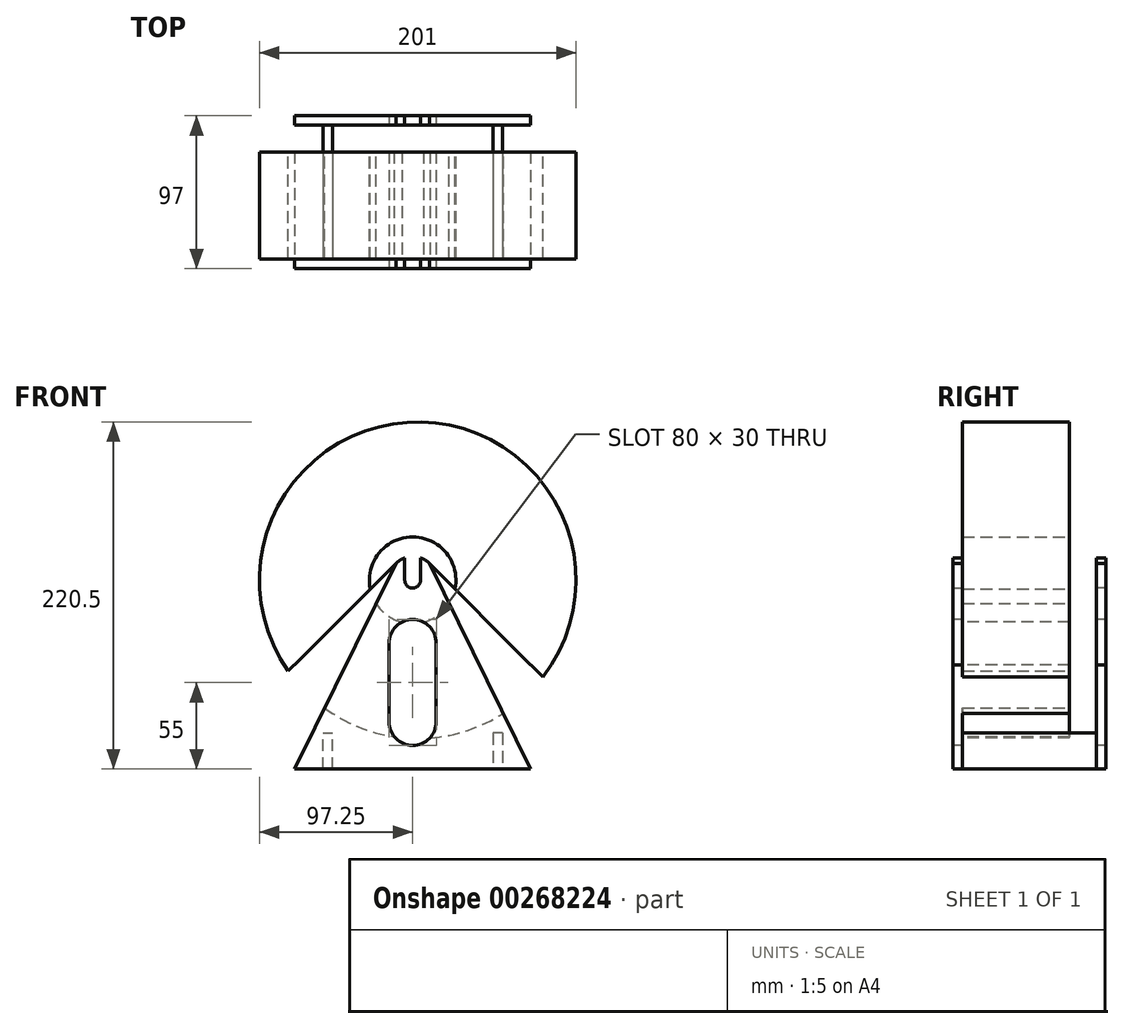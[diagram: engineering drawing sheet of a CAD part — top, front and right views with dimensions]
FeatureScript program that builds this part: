
annotation { "Feature Type Name" : "Feature", "Feature Type Description" : "" }
export const myFeature = defineFeature(function(context is Context, id is Id, definition is map)
    precondition{}
    {
        {
            var Q0;
            Q0=qCreatedBy(makeId("Front.planeOp"),FACE);
            var sketch = newSketch(context, id + "F0", { "sketchPlane" : qUnion([Q0])});
            skCircle(sketch, "E0", {"center": v(0, 0) * mm, "radius": 27.5 * mm});
            skCircle(sketch, "E1", {"center": v(3.25, 0) * mm, "radius": 100.5 * mm});
            skSolve(sketch);
        }
        {
            var Q0;
            Q0=makeQuery(id+"F0.imprint","IMPRINT",FACE,{"disambiguationData":[TD([[makeQuery(id+"F0.imprint","IMPRINT",EDGE,{"derivedFrom":sQuery(id+"F0.wireOp",EDGE,"E0")}),-1.0]])]});
            extrude(context, id + "F1", {"entities" : qUnion([Q0]), "endBound" : BoundingType.SYMMETRIC, "depth" : 68 * mm});
        }
        {
            var Q0;
            Q0=makeQuery(id+"F1.opExtrude","CAP_FACE",FACE,{"disambiguationData":[OSD([sQuery(id+"F0.wireOp",EDGE,"E0"),sQuery(id+"F0.wireOp",EDGE,"E1")])],"isStart":false});
            var sketch = newSketch(context, id + "F2", { "sketchPlane" : qUnion([Q0])});
            skArc(sketch, "E2", {"start": v(-5, 14.23) * mm, "mid": v(-8.03, 12.77) * mm, "end": v(-10.67, 10.67) * mm});
            skArc(sketch, "E3", {"start": v(-5, 0) * mm, "mid": v(0, -5) * mm, "end": v(5, 0) * mm});
            skLineSegment(sketch, "E4", {"start": v(0, 0) * mm, "end": v(5, 0) * mm});
            skLineSegment(sketch, "E5", {"start": v(5, 0) * mm, "end": v(5, 14.23) * mm});
            skLineSegment(sketch, "E6", {"start": v(0, 0) * mm, "end": v(-5, 0) * mm});
            skLineSegment(sketch, "E7", {"start": v(-5, 0) * mm, "end": v(-5, 14.23) * mm});
            skLineSegment(sketch, "E8", {"start": v(-10.67, 10.67) * mm, "end": v(-141.33, -120) * mm});
            skLineSegment(sketch, "E9", {"start": v(-141.33, -120) * mm, "end": v(141.33, -120) * mm});
            skLineSegment(sketch, "E10", {"start": v(141.33, -120) * mm, "end": v(10.67, 10.67) * mm});
            skArc(sketch, "E11.trimOffspring", {"start": v(10.67, 10.67) * mm, "mid": v(8.03, 12.77) * mm, "end": v(5, 14.23) * mm});
            skSolve(sketch);
        }
        {
            var Q0;
            {var subQ0=sQuery(id+"F2.wireOp",EDGE,"E9");Q0=makeQuery(id+"F2.imprint","IMPRINT",FACE,{"disambiguationData":[TD([[makeQuery(id+"F2.imprint","IMPRINT",EDGE,{"derivedFrom":subQ0}),1.0]])]});}
            var Q1;
            {var subQ0=sQuery(id+"F2.wireOp",EDGE,"E8");var subQ1=makeQuery(id+"F1.opExtrude","CAP_EDGE",EDGE,{"disambiguationData":[OSD([sQuery(id+"F0.wireOp",EDGE,"E1")])],"isStart":false});var subQ2=makeQuery(id+"F2.imprint","INTERSECT",VERTEX,{"derivedFrom":[subQ1,subQ0]});Q1=makeQuery(id+"F2.imprint","IMPRINT",FACE,{"disambiguationData":[TD([[makeQuery(id+"F2.imprint","IMPRINT",EDGE,{"disambiguationData":[TD([[subQ2,1.0]])],"derivedFrom":subQ0}),1.0]])]});}
            var Q2;
            {var subQ0=sQuery(id+"F2.wireOp",EDGE,"E2");Q2=makeQuery(id+"F2.imprint","IMPRINT",FACE,{"disambiguationData":[TD([[makeQuery(id+"F2.imprint","IMPRINT",EDGE,{"derivedFrom":subQ0}),1.0]])]});}
            extrude(context, id + "F3", {"entities" : qUnion([Q0, Q1, Q2]), "depth" : 6 * mm});
        }
        {
            var Q0;
            Q0=makeQuery(id+"F3.opExtrude","CAP_FACE",FACE,{"disambiguationData":[OSD([sQuery(id+"F2.wireOp",EDGE,"E2"),sQuery(id+"F2.wireOp",EDGE,"E3"),sQuery(id+"F2.wireOp",EDGE,"E5"),sQuery(id+"F2.wireOp",EDGE,"E7"),sQuery(id+"F2.wireOp",EDGE,"E8"),sQuery(id+"F2.wireOp",EDGE,"E9"),sQuery(id+"F2.wireOp",EDGE,"E10"),sQuery(id+"F2.wireOp",EDGE,"E11.trimOffspring")])],"isStart":true});
            var sketch = newSketch(context, id + "F4", { "sketchPlane" : qUnion([Q0])});
            skLineSegment(sketch, "E12.bottom", {"start": v(-75, -120) * mm, "end": v(75, -120) * mm});
            skLineSegment(sketch, "E12.top", {"start": v(-75, -114) * mm, "end": v(75, -114) * mm});
            skLineSegment(sketch, "E12.left", {"start": v(-75, -120) * mm, "end": v(-75, -114) * mm});
            skLineSegment(sketch, "E12.right", {"start": v(75, -120) * mm, "end": v(75, -114) * mm});
            skSolve(sketch);
        }
        {
            var Q0;
            Q0=makeQuery(id+"F4.imprint","IMPRINT",FACE,{"disambiguationData":[TD([[makeQuery(id+"F4.imprint","IMPRINT",EDGE,{"derivedFrom":sQuery(id+"F4.wireOp",EDGE,"E12.bottom")}),-1.0]])]});
            extrude(context, id + "F5", {"entities" : qUnion([Q0]), "operationType" : NewBodyOperationType.ADD, "depth" : 85 * mm});
        }
        {
            var Q0;
            Q0=makeQuery(id+"F3.opExtrude","CAP_FACE",FACE,{"disambiguationData":[OSD([sQuery(id+"F2.wireOp",EDGE,"E2"),sQuery(id+"F2.wireOp",EDGE,"E3"),sQuery(id+"F2.wireOp",EDGE,"E5"),sQuery(id+"F2.wireOp",EDGE,"E7"),sQuery(id+"F2.wireOp",EDGE,"E8"),sQuery(id+"F2.wireOp",EDGE,"E9"),sQuery(id+"F2.wireOp",EDGE,"E10"),sQuery(id+"F2.wireOp",EDGE,"E11.trimOffspring")])],"isStart":true});
            var Q1;
            Q1=makeQuery(id+"F5.opExtrude","CAP_FACE",FACE,{"disambiguationData":[OSD([sQuery(id+"F4.wireOp",EDGE,"E12.bottom"),sQuery(id+"F4.wireOp",EDGE,"E12.top"),sQuery(id+"F4.wireOp",EDGE,"E12.left"),sQuery(id+"F4.wireOp",EDGE,"E12.right")])],"isStart":false});
            cPlane(context, id + "F6", {"entities" : qUnion([Q0, Q1]), "cplaneType" : CPlaneType.MID_PLANE, "offset" : 25 * mm, "width" : 150 * mm, "height" : 150 * mm});
        }
        {
            var Q0;
            Q0=makeQuery(id+"F3.opExtrude","SWEPT_BODY",BODY,{"disambiguationData":[OSD([sQuery(id+"F2.wireOp",EDGE,"E2"),sQuery(id+"F2.wireOp",EDGE,"E3"),sQuery(id+"F2.wireOp",EDGE,"E5"),sQuery(id+"F2.wireOp",EDGE,"E7"),sQuery(id+"F2.wireOp",EDGE,"E8"),sQuery(id+"F2.wireOp",EDGE,"E9"),sQuery(id+"F2.wireOp",EDGE,"E10"),sQuery(id+"F2.wireOp",EDGE,"E11.trimOffspring")])]});
            var Q1;
            Q1=qCreatedBy(id+"F6.planeOp",FACE);
            mirror(context, id + "F7", {"operationType" : NewBodyOperationType.ADD, "entities" : qUnion([Q0]), "mirrorPlane" : qUnion([Q1])});
        }
        {
            var Q0;
            Q0=makeQuery(id+"F3.opExtrude","CAP_FACE",FACE,{"disambiguationData":[OSD([sQuery(id+"F2.wireOp",EDGE,"E2"),sQuery(id+"F2.wireOp",EDGE,"E3"),sQuery(id+"F2.wireOp",EDGE,"E5"),sQuery(id+"F2.wireOp",EDGE,"E7"),sQuery(id+"F2.wireOp",EDGE,"E8"),sQuery(id+"F2.wireOp",EDGE,"E9"),sQuery(id+"F2.wireOp",EDGE,"E10"),sQuery(id+"F2.wireOp",EDGE,"E11.trimOffspring")])],"isStart":false});
            var sketch = newSketch(context, id + "F8", { "sketchPlane" : qUnion([Q0])});
            skLineSegment(sketch, "E13.bottom", {"start": v(-75, -120) * mm, "end": v(-147.4, -120) * mm});
            skLineSegment(sketch, "E13.top", {"start": v(-75, -40) * mm, "end": v(-147.4, -40) * mm});
            skLineSegment(sketch, "E13.left", {"start": v(-75, -120) * mm, "end": v(-75, -40) * mm});
            skLineSegment(sketch, "E13.right", {"start": v(-147.4, -120) * mm, "end": v(-147.4, -40) * mm});
            skLineSegment(sketch, "E14.bottom", {"start": v(75, -120) * mm, "end": v(157.32, -120) * mm});
            skLineSegment(sketch, "E14.top", {"start": v(75, -28.86) * mm, "end": v(157.32, -28.86) * mm});
            skLineSegment(sketch, "E14.left", {"start": v(75, -120) * mm, "end": v(75, -28.86) * mm});
            skLineSegment(sketch, "E14.right", {"start": v(157.32, -120) * mm, "end": v(157.32, -28.86) * mm});
            skArc(sketch, "E15", {"start": v(15, -40) * mm, "mid": v(0, -25) * mm, "end": v(-15, -40) * mm});
            skArc(sketch, "E16", {"start": v(-15, -90) * mm, "mid": v(0, -105) * mm, "end": v(15, -90) * mm});
            skLineSegment(sketch, "E17", {"start": v(-15, -40) * mm, "end": v(-15, -90) * mm});
            skLineSegment(sketch, "E18", {"start": v(15, -40) * mm, "end": v(15, -90) * mm});
            skLineSegment(sketch, "E19", {"start": v(-75, -120) * mm, "end": v(-10.67, 10.67) * mm});
            skPoint(sketch, "E20.endSnap0", {"position": v(-76, -54.67) * mm});
            skLineSegment(sketch, "E21", {"start": v(-75, -54.67) * mm, "end": v(-75, -120) * mm});
            skLineSegment(sketch, "E22", {"start": v(75, -120) * mm, "end": v(10.67, 10.67) * mm});
            skLineSegment(sketch, "E23", {"start": v(10.67, 10.67) * mm, "end": v(75, -53.67) * mm});
            skLineSegment(sketch, "E24", {"start": v(75, -53.67) * mm, "end": v(75, -120) * mm});
            skLineSegment(sketch, "E25", {"start": v(-10.67, 10.67) * mm, "end": v(-75, -53.67) * mm});
            skLineSegment(sketch, "E26", {"start": v(-75, -53.67) * mm, "end": v(-75, -54.67) * mm});
            skSolve(sketch);
        }
        {
            var Q0;
            Q0=makeQuery(id+"F8.imprint","IMPRINT",FACE,{"disambiguationData":[TD([[makeQuery(id+"F8.imprint","IMPRINT",EDGE,{"derivedFrom":sQuery(id+"F8.wireOp",EDGE,"ZRvT6IEv-0Fsf-O5qo-igZU-xmLnPdFTF6ZU")}),1.0]])]});
            var Q1;
            {var subQ0=sQuery(id+"F8.wireOp",EDGE,"E13.bottom");var subQ1=makeQuery(id+"F3.opExtrude","CAP_EDGE",EDGE,{"disambiguationData":[OSD([sQuery(id+"F2.wireOp",EDGE,"E8")])],"isStart":false});var subQ2=makeQuery(id+"F8.imprint","INTERSECT",VERTEX,{"derivedFrom":[subQ1,subQ0]});Q1=makeQuery(id+"F8.imprint","IMPRINT",FACE,{"disambiguationData":[TD([[makeQuery(id+"F8.imprint","IMPRINT",EDGE,{"disambiguationData":[TD([[subQ2,1.0]])],"derivedFrom":subQ1}),1.0]])]});}
            var Q2;
            {var subQ0=sQuery(id+"F8.wireOp",EDGE,"E14.bottom");var subQ1=makeQuery(id+"F3.opExtrude","CAP_EDGE",EDGE,{"disambiguationData":[OSD([sQuery(id+"F2.wireOp",EDGE,"E10")])],"isStart":false});var subQ2=makeQuery(id+"F8.imprint","INTERSECT",VERTEX,{"derivedFrom":[subQ1,subQ0]});Q2=makeQuery(id+"F8.imprint","IMPRINT",FACE,{"disambiguationData":[TD([[makeQuery(id+"F8.imprint","IMPRINT",EDGE,{"disambiguationData":[TD([[subQ2,-1.0]])],"derivedFrom":subQ1}),1.0]])]});}
            var Q3;
            Q3=makeQuery(id+"F8.imprint","IMPRINT",FACE,{"disambiguationData":[TD([[makeQuery(id+"F8.imprint","IMPRINT",EDGE,{"derivedFrom":sQuery(id+"F8.wireOp",EDGE,"E15")}),1.0]])]});
            var Q4;
            Q4=makeQuery(id+"F8.imprint","IMPRINT",FACE,{"disambiguationData":[TD([[makeQuery(id+"F8.imprint","IMPRINT",EDGE,{"derivedFrom":sQuery(id+"F8.wireOp",EDGE,"E19")}),1.0]])]});
            var Q5;
            Q5=makeQuery(id+"F8.imprint","IMPRINT",FACE,{"disambiguationData":[TD([[makeQuery(id+"F8.imprint","IMPRINT",EDGE,{"derivedFrom":sQuery(id+"F8.wireOp",EDGE,"E22")}),-1.0]])]});
            extrude(context, id + "F9", {"entities" : qUnion([Q0, Q1, Q2, Q3, Q4, Q5]), "operationType" : NewBodyOperationType.REMOVE, "oppositeDirection" : true, "depth" : 122 * mm});
        }
        {
            var Q0;
            Q0=makeQuery(id+"F5.opExtrude","CAP_EDGE",EDGE,{"disambiguationData":[OSD([sQuery(id+"F4.wireOp",EDGE,"E12.top")])],"isStart":true});
            var Q1;
            {var subQ0=sQuery(id+"F4.wireOp",EDGE,"E12.top");Q1=makeQuery(id+"F7.boolean.opBoolean","MERGE",EDGE,{"derivedFrom":[makeQuery(id+"F5.opExtrude","CAP_EDGE",EDGE,{"disambiguationData":[OSD([subQ0])],"isStart":false}),makeQuery(id+"F7.opPattern","COPY",EDGE,{"derivedFrom":makeQuery(id+"F5.opExtrude","CAP_EDGE",EDGE,{"disambiguationData":[OSD([subQ0])],"isStart":true}),"instanceName":"1"})]});}
            fillet(context, id + "F10", {"entities" : qUnion([Q0, Q1]), "radius" : 5 * mm, "tangentPropagation" : true, "allowEdgeOverflow" : false});
        }
        {
            var Q0;
            {var subQ1=sQuery(id+"F2.wireOp",EDGE,"E10");var subQ8=sQuery(id+"F8.wireOp",EDGE,"E14.left");Q0=makeQuery(id+"F9.boolean.opBoolean","COPY",EDGE,{"disambiguationData":[TD([makeQuery(id+"F7.opPattern","COPY",FACE,{"derivedFrom":makeQuery(id+"F3.opExtrude","SWEPT_FACE",FACE,{"disambiguationData":[OSD([subQ1])]}),"instanceName":"1"})])],"derivedFrom":makeQuery(id+"F9.opExtrude","SWEPT_EDGE",EDGE,{"disambiguationData":[OSD([subQ1,subQ8])]})});}
            var Q1;
            {var subQ3=sQuery(id+"F2.wireOp",EDGE,"E8");var subQ8=sQuery(id+"F8.wireOp",EDGE,"E13.left");Q1=makeQuery(id+"F9.boolean.opBoolean","COPY",EDGE,{"disambiguationData":[TD([makeQuery(id+"F7.opPattern","COPY",FACE,{"derivedFrom":makeQuery(id+"F3.opExtrude","SWEPT_FACE",FACE,{"disambiguationData":[OSD([subQ3])]}),"instanceName":"1"})])],"derivedFrom":makeQuery(id+"F9.opExtrude","SWEPT_EDGE",EDGE,{"disambiguationData":[OSD([subQ3,subQ8])]})});}
            var Q2;
            {var subQ0=sQuery(id+"F2.wireOp",EDGE,"E8");var subQ8=sQuery(id+"F8.wireOp",EDGE,"E13.left");Q2=makeQuery(id+"F9.boolean.opBoolean","COPY",EDGE,{"disambiguationData":[TD([makeQuery(id+"F3.opExtrude","SWEPT_FACE",FACE,{"disambiguationData":[OSD([subQ0])]})])],"derivedFrom":makeQuery(id+"F9.opExtrude","SWEPT_EDGE",EDGE,{"disambiguationData":[OSD([subQ0,subQ8])]})});}
            var Q3;
            {var subQ0=sQuery(id+"F2.wireOp",EDGE,"E10");var subQ8=sQuery(id+"F8.wireOp",EDGE,"E14.left");Q3=makeQuery(id+"F9.boolean.opBoolean","COPY",EDGE,{"disambiguationData":[TD([makeQuery(id+"F3.opExtrude","SWEPT_FACE",FACE,{"disambiguationData":[OSD([subQ0])]})])],"derivedFrom":makeQuery(id+"F9.opExtrude","SWEPT_EDGE",EDGE,{"disambiguationData":[OSD([subQ0,subQ8])]})});}
            fillet(context, id + "F11", {"entities" : qUnion([Q0, Q1, Q2, Q3]), "radius" : 10 * mm, "tangentPropagation" : true, "allowEdgeOverflow" : false});
        }
        {
            var Q0;
            Q0=qCreatedBy(makeId("Right.planeOp"),FACE);
            var sketch = newSketch(context, id + "F12", { "sketchPlane" : qUnion([Q0])});
            skLineSegment(sketch, "E27.bottom", {"start": v(-34, -104.24) * mm, "end": v(51, -104.24) * mm});
            skLineSegment(sketch, "E27.top", {"start": v(-34, -140.47) * mm, "end": v(51, -140.47) * mm});
            skLineSegment(sketch, "E27.left", {"start": v(-34, -104.24) * mm, "end": v(-34, -140.47) * mm});
            skLineSegment(sketch, "E27.right", {"start": v(51, -104.24) * mm, "end": v(51, -140.47) * mm});
            skSolve(sketch);
        }
        {
            var Q0;
            Q0=makeQuery(id+"F12.imprint","IMPRINT",FACE,{"disambiguationData":[TD([[makeQuery(id+"F12.imprint","IMPRINT",EDGE,{"derivedFrom":sQuery(id+"F12.wireOp",EDGE,"E27.bottom")}),-1.0]])]});
            extrude(context, id + "F13", {"entities" : qUnion([Q0]), "operationType" : NewBodyOperationType.REMOVE, "endBound" : BoundingType.SYMMETRIC, "oppositeDirection" : true, "depth" : 344 * mm});
        }
        {
            var Q0;
            Q0=makeQuery(id+"F13.boolean.opBoolean","MERGE",FACE,{"derivedFrom":[makeQuery(id+"F3.opExtrude","CAP_FACE",FACE,{"disambiguationData":[OSD([sQuery(id+"F2.wireOp",EDGE,"E2"),sQuery(id+"F2.wireOp",EDGE,"E3"),sQuery(id+"F2.wireOp",EDGE,"E5"),sQuery(id+"F2.wireOp",EDGE,"E7"),sQuery(id+"F2.wireOp",EDGE,"E8"),sQuery(id+"F2.wireOp",EDGE,"E9"),sQuery(id+"F2.wireOp",EDGE,"E10"),sQuery(id+"F2.wireOp",EDGE,"E11.trimOffspring")])],"isStart":true}),makeQuery(id+"F13.opExtrude","SWEPT_FACE",FACE,{"disambiguationData":[OSD([sQuery(id+"F12.wireOp",EDGE,"E27.left")])]})]});
            var sketch = newSketch(context, id + "F14", { "sketchPlane" : qUnion([Q0])});
            skLineSegment(sketch, "E28.bottom", {"start": v(-57, -97) * mm, "end": v(-51, -97) * mm});
            skLineSegment(sketch, "E28.top", {"start": v(-57, -120) * mm, "end": v(-51, -120) * mm});
            skLineSegment(sketch, "E28.left", {"start": v(-57, -97) * mm, "end": v(-57, -120) * mm});
            skLineSegment(sketch, "E28.right", {"start": v(-51, -97) * mm, "end": v(-51, -120) * mm});
            skLineSegment(sketch, "E29.bottom", {"start": v(57, -120) * mm, "end": v(51, -120) * mm});
            skLineSegment(sketch, "E29.top", {"start": v(57, -97) * mm, "end": v(51, -97) * mm});
            skLineSegment(sketch, "E29.left", {"start": v(57, -120) * mm, "end": v(57, -97) * mm});
            skLineSegment(sketch, "E29.right", {"start": v(51, -120) * mm, "end": v(51, -97) * mm});
            skSolve(sketch);
        }
        {
            var Q0;
            Q0=makeQuery(id+"F14.imprint","IMPRINT",FACE,{"disambiguationData":[TD([[makeQuery(id+"F14.imprint","IMPRINT",EDGE,{"derivedFrom":sQuery(id+"F14.wireOp",EDGE,"E28.bottom")}),-1.0]])]});
            var Q1;
            Q1=makeQuery(id+"F14.imprint","IMPRINT",FACE,{"disambiguationData":[TD([[makeQuery(id+"F14.imprint","IMPRINT",EDGE,{"derivedFrom":sQuery(id+"F14.wireOp",EDGE,"E29.bottom")}),-1.0]])]});
            var Q2;
            Q2=makeQuery(id+"F13.boolean.opBoolean","MERGE",FACE,{"derivedFrom":[makeQuery(id+"F7.opPattern","COPY",FACE,{"derivedFrom":makeQuery(id+"F3.opExtrude","CAP_FACE",FACE,{"disambiguationData":[OSD([sQuery(id+"F2.wireOp",EDGE,"E2"),sQuery(id+"F2.wireOp",EDGE,"E3"),sQuery(id+"F2.wireOp",EDGE,"E5"),sQuery(id+"F2.wireOp",EDGE,"E7"),sQuery(id+"F2.wireOp",EDGE,"E8"),sQuery(id+"F2.wireOp",EDGE,"E9"),sQuery(id+"F2.wireOp",EDGE,"E10"),sQuery(id+"F2.wireOp",EDGE,"E11.trimOffspring")])],"isStart":true}),"instanceName":"1"}),makeQuery(id+"F13.opExtrude","SWEPT_FACE",FACE,{"disambiguationData":[OSD([sQuery(id+"F12.wireOp",EDGE,"E27.right")])]})]});
            extrude(context, id + "F15", {"entities" : qUnion([Q0, Q1]), "operationType" : NewBodyOperationType.ADD, "endBound" : BoundingType.UP_TO_SURFACE, "endBoundEntityFace" : qUnion([Q2]), "depth" : 25 * mm});
        }
    });
